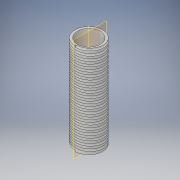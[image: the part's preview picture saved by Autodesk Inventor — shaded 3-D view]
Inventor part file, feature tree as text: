
AUTODESK INVENTOR PART (.ipt)
format: ipt  version: 2019.2 (Build 232265000, 265)  size: 492,032 bytes
history: native  units: in
note: dims shown in document units (in); Inventor stores cm internally (conversion verified against a paired STEP export)
features: sketch x3, extrude x2, helix x1
ambient origin geometry x8: Origin, YZ Plane, XZ Plane, XY Plane, X Axis, Y Axis, Z Axis, Center Point
bodies: Solid1 (feature_tree)
feature tree (6):
  extrude  "Extrusion1"  Depth=5.0in
  helix  "Coil1"  [1 undecoded]
  extrude  "Extrusion3"  Depth=2.0in TaperAngle=0.0deg
  sketch  "Sketch1"  dims[d0=5.0in d1=0.0in d4=1.25in d5=1.5in]
  sketch  "Sketch2"  dims[d10=0.25in d11=1.0in d12=7.874in d13=0.0in d14=90.0deg d15=90.0deg d16=0.0in d17=0.0in d18=0.125in d21=2.0in d22=0.0in]
  sketch  "Sketch4"
note: 1 required parameter value undecoded (feature->parameter linkage not recoverable at this tier; creation-order binding heuristic only, values carry confidence <= 0.55)
